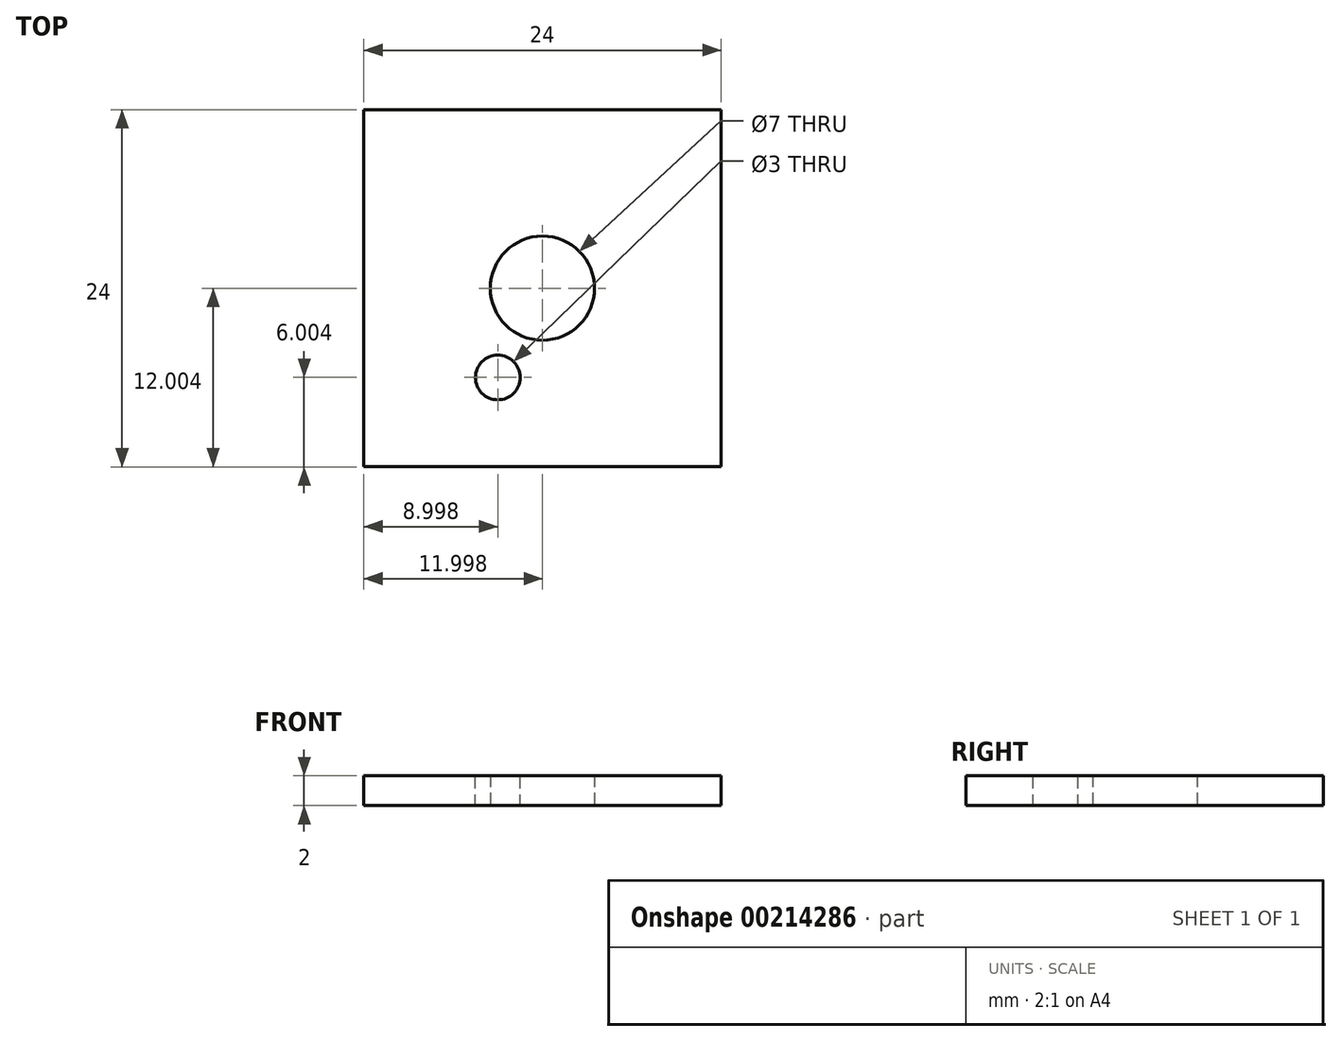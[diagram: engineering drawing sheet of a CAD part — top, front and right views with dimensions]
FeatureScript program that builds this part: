
annotation { "Feature Type Name" : "Feature", "Feature Type Description" : "" }
export const myFeature = defineFeature(function(context is Context, id is Id, definition is map)
    precondition{}
    {
        {
            var Q0;
            Q0=qCreatedBy(makeId("Top.planeOp"),FACE);
            var sketch = newSketch(context, id + "F0", { "sketchPlane" : qUnion([Q0])});
            skLineSegment(sketch, "E0.bottom", {"start": v(4.1, -2.38) * mm, "end": v(28.1, -2.38) * mm});
            skLineSegment(sketch, "E0.top", {"start": v(4.1, -26.38) * mm, "end": v(28.1, -26.38) * mm});
            skLineSegment(sketch, "E0.left", {"start": v(4.1, -2.38) * mm, "end": v(4.1, -26.38) * mm});
            skLineSegment(sketch, "E0.right", {"start": v(28.1, -2.38) * mm, "end": v(28.1, -26.38) * mm});
            skCircle(sketch, "E1", {"center": v(16.1, -14.38) * mm, "radius": 3.5 * mm});
            skSolve(sketch);
        }
        {
            var Q0;
            Q0 = qSketchRegion(id + "F0", true);
            extrude(context, id + "F1", {"entities" : qUnion([Q0]), "depth" : 2 * mm});
        }
        {
            var Q0;
            Q0=makeQuery(id+"F1.opExtrude","CAP_FACE",FACE,{"disambiguationData":[OSD([sQuery(id+"F0.wireOp",EDGE,"E0.bottom"),sQuery(id+"F0.wireOp",EDGE,"E0.top"),sQuery(id+"F0.wireOp",EDGE,"E0.left"),sQuery(id+"F0.wireOp",EDGE,"E0.right"),sQuery(id+"F0.wireOp",EDGE,"E1")])],"isStart":false});
            var sketch = newSketch(context, id + "F2", { "sketchPlane" : qUnion([Q0])});
            skCircle(sketch, "E2", {"center": v(13.1, -20.38) * mm, "radius": 1.5 * mm});
            skSolve(sketch);
        }
        {
            var Q0;
            Q0 = qSketchRegion(id + "F2", true);
            extrude(context, id + "F3", {"entities" : qUnion([Q0]), "operationType" : NewBodyOperationType.REMOVE, "oppositeDirection" : true, "depth" : 25 * mm});
        }
    });
